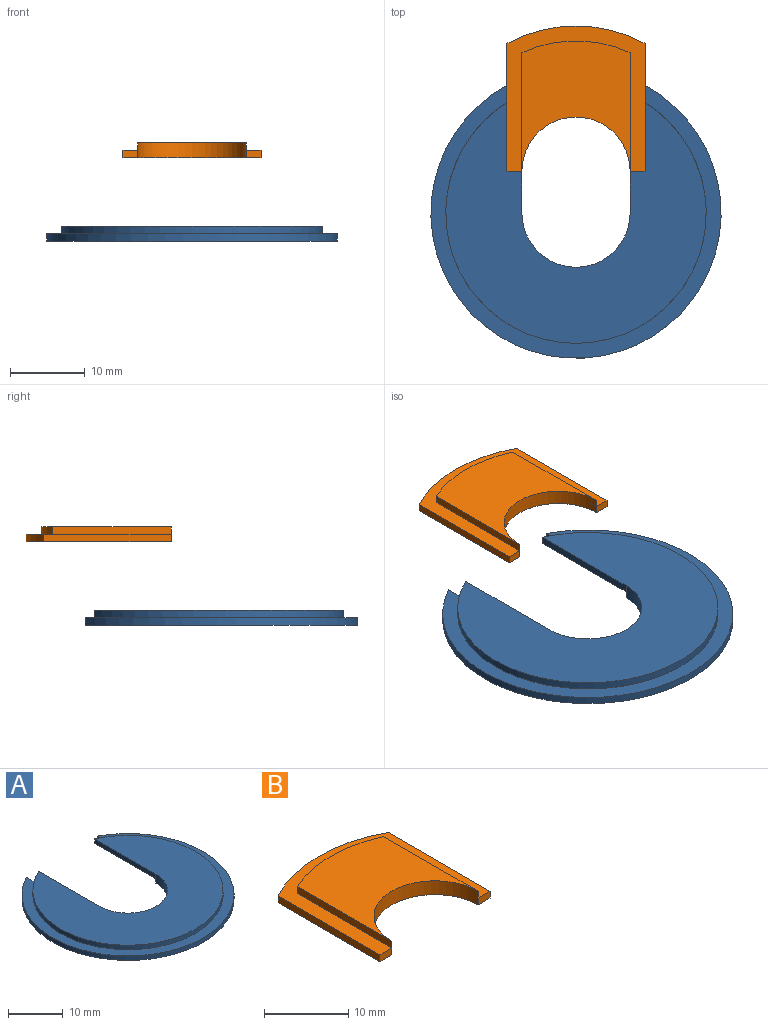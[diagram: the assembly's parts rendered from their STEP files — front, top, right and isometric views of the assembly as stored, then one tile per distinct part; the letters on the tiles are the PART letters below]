
ASSEMBLY  parts=2 mates=1
PART A: 14 faces, bbox 38.9x36.6x2 mm
  f0: plane 2x1mm, normal (0,1,0), area 2mm2, adj f1,f5,f7,f13
  f1: plane 17.11x1mm, normal (1,0,0), area 17.1mm2, adj f0,f7,f8,f9,f13
  f2: plane 2x1mm, normal (0,1,0), area 2mm2, adj f3,f5,f7,f11
  f3: plane 17.11x1mm, normal (-1,0,0), area 17.1mm2, adj f2,f7,f8,f9,f11
  f4: cylinder r=17.45mm len=34.9mm, axis (0,0,-1), area 94.7mm2, adj f6,f9,f10,f11,f12,f13
  f5: cylinder r=7.25mm len=14.5mm, axis (0,0,-1), area 45.6mm2, adj f0,f2,f6,f7,f10,f12
  f6: plane 34.9x33.32mm, normal (0,0,1), area 628.5mm2, adj f4,f5,f10,f12
  f7: plane 38.9x36.56mm, normal (0,0,-1), area 760.1mm2, adj f0,f1,f2,f3,f5,f8
  f8: cylinder r=19.45mm len=38.9mm, axis (0,0,-1), area 102.9mm2, adj f1,f3,f7,f9
  f9: plane 38.9x36.56mm, normal (0,0,1), area 193.1mm2, adj f1,f3,f4,f8
  f10: plane 15.87x1mm, normal (-1,0,0), area 15.9mm2, adj f4,f5,f6,f11
  f11: plane 15.87x2mm, normal (0,0,-1), area 30.7mm2, adj f2,f3,f4,f10
  f12: plane 15.87x1mm, normal (1,0,0), area 15.9mm2, adj f4,f5,f6,f13
  f13: plane 15.87x2mm, normal (0,0,-1), area 30.7mm2, adj f0,f1,f4,f12
PART B: 12 faces, bbox 18.5x19.5x2 mm
  f0: plane 15.87x1mm, normal (-1,0,0), area 15.9mm2, adj f1,f3,f4,f11
  f1: cylinder r=7.25mm len=14.5mm, axis (0,0,-1), area 45.6mm2, adj f0,f2,f4,f5,f9,f10
  f2: plane 15.87x1mm, normal (1,0,0), area 15.9mm2, adj f1,f3,f4,f11
  f3: cylinder r=17.45mm len=14.5mm, axis (0,0,-1), area 15mm2, adj f0,f2,f4,f11
  f4: plane 17.45x14.5mm, normal (0,0,1), area 163mm2, adj f0,f1,f2,f3
  f5: plane 19.45x18.5mm, normal (0,0,-1), area 263.2mm2, adj f1,f6,f7,f8,f9,f10
  f6: plane 17.11x1mm, normal (1,0,0), area 17.1mm2, adj f5,f7,f10,f11
  f7: cylinder r=19.45mm len=18.5mm, axis (0,0,-1), area 19.3mm2, adj f5,f6,f8,f11
  f8: plane 17.11x1mm, normal (-1,0,0), area 17.1mm2, adj f5,f7,f9,f11
  f9: plane 2x1mm, normal (0,-1,0), area 2mm2, adj f1,f5,f8,f11
  f10: plane 2x1mm, normal (0,-1,0), area 2mm2, adj f1,f5,f6,f11
  f11: plane 19.45x18.5mm, normal (0,0,1), area 100.2mm2, adj f0,f2,f3,f6,f7,f8,f9,f10
PLACE A t=(13.84,6.48,6.48)mm
PLACE B t=(13.84,12.08,17.64)mm
MATE planar B.f6 <-> A.f3  axis (1,0,0) through (23.09,20.64,18.14)mm
